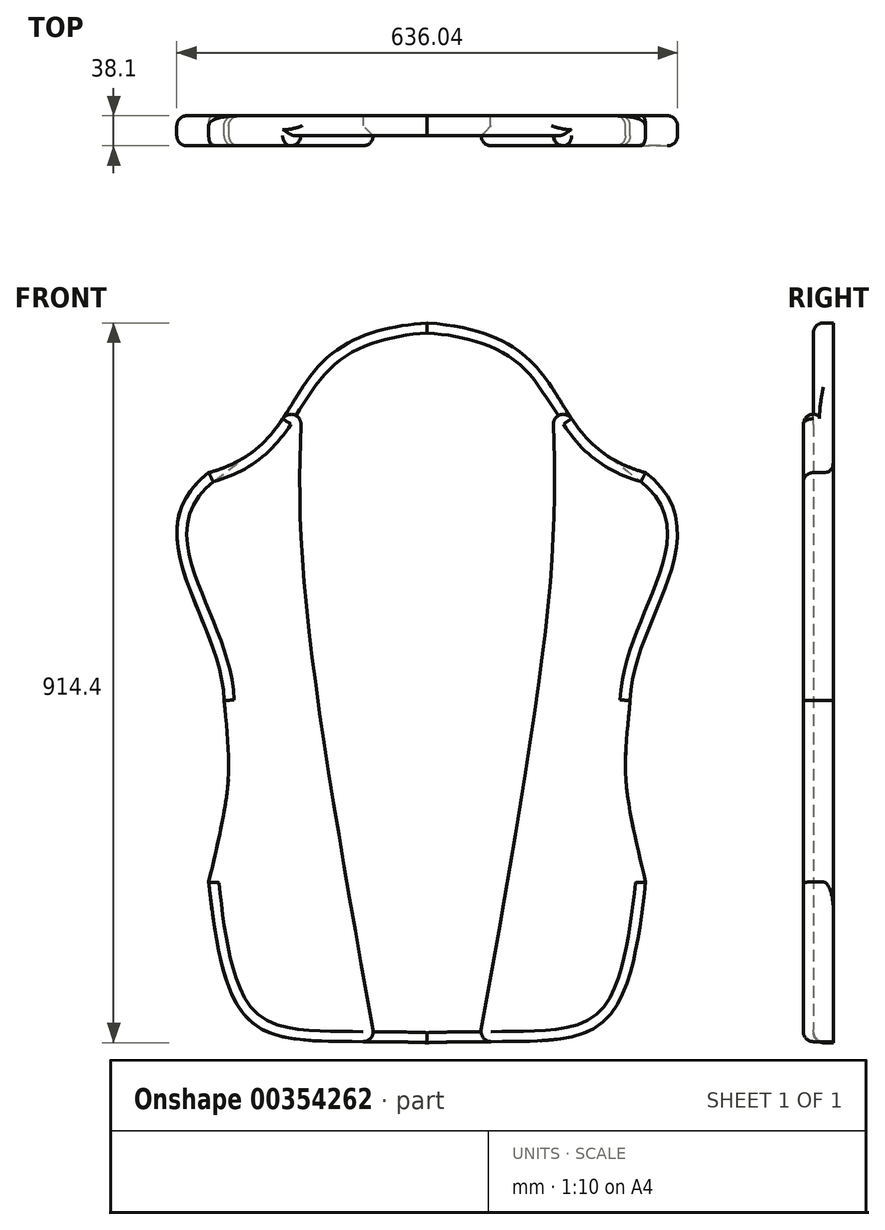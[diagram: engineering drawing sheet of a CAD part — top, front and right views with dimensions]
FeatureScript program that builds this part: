
annotation { "Feature Type Name" : "Feature", "Feature Type Description" : "" }
export const myFeature = defineFeature(function(context is Context, id is Id, definition is map)
    precondition{}
    {
        {
            var Q0;
            Q0=qCreatedBy(makeId("Front.planeOp"),FACE);
            var sketch = newSketch(context, id + "F0", { "sketchPlane" : qUnion([Q0])});
            skFitSpline(sketch, "E0", {"points": [v(0, -336.62) * mm, v(-277.45, -132.55) * mm], "startDerivative": vector(-633.05, 22.6) * mm, "endDerivative": vector(-75.36, 708.4) * mm});
            skFitSpline(sketch, "E1", {"points": [v(-277.45, -132.55) * mm, v(-257.9, 97.97) * mm], "startDerivative": vector(90.44, 384.35) * mm, "endDerivative": vector(-28.5, 293.91) * mm});
            skFitSpline(sketch, "E2", {"points": [v(-257.9, 97.97) * mm, v(-277.45, 387.49) * mm], "startDerivative": vector(-7.54, 308.99) * mm, "endDerivative": vector(301.45, 233.62) * mm});
            skFitSpline(sketch, "E3", {"points": [v(-277.45, 387.49) * mm, v(0, 577.78) * mm], "startDerivative": vector(428.8, 118.6) * mm, "endDerivative": vector(606.67, 45.22) * mm});
            skLineSegment(sketch, "E4", {"start": v(0, 700.87) * mm, "end": v(0, -462.22) * mm, "construction": true});
            skFitSpline(sketch, "E5.MirrorCS", {"points": [v(277.45, 387.49) * mm, v(0, 577.78) * mm], "startDerivative": vector(-428.8, 118.6) * mm, "endDerivative": vector(-606.67, 45.22) * mm});
            skFitSpline(sketch, "E6.MirrorCS", {"points": [v(257.9, 97.97) * mm, v(277.45, 387.49) * mm], "startDerivative": vector(7.54, 308.99) * mm, "endDerivative": vector(-301.45, 233.62) * mm});
            skFitSpline(sketch, "E7.MirrorCS", {"points": [v(277.45, -132.55) * mm, v(257.9, 97.97) * mm], "startDerivative": vector(-90.44, 384.35) * mm, "endDerivative": vector(28.5, 293.91) * mm});
            skFitSpline(sketch, "E8.MirrorCS", {"points": [v(0, -336.62) * mm, v(277.45, -132.55) * mm], "startDerivative": vector(633.05, 22.6) * mm, "endDerivative": vector(75.36, 708.4) * mm});
            skFitSpline(sketch, "E9", {"points": [v(-158.07, 496.23) * mm, v(-157.28, 260.19) * mm, v(-66.01, -335.4) * mm], "startDerivative": vector(-27, -544.47) * mm, "endDerivative": vector(193.6, -1077.9) * mm});
            skFitSpline(sketch, "E10.MirrorCS", {"points": [v(158.07, 496.23) * mm, v(157.28, 260.19) * mm, v(66.01, -335.4) * mm], "startDerivative": vector(27, -544.47) * mm, "endDerivative": vector(-193.6, -1077.9) * mm});
            skSolve(sketch);
        }
        {
            var Q0;
            {var subQ7=sQuery(id+"F0.wireOp",EDGE,"E9");Q0=makeQuery(id+"F0.imprint","IMPRINT",FACE,{"disambiguationData":[TD([[makeQuery(id+"F0.imprint","IMPRINT",EDGE,{"derivedFrom":subQ7}),1.0]])]});}
            extrude(context, id + "F1", {"entities" : qUnion([Q0]), "depth" : 25.4 * mm});
        }
        {
            var Q0;
            {var subQ3=sQuery(id+"F0.wireOp",EDGE,"E1");Q0=makeQuery(id+"F0.imprint","IMPRINT",FACE,{"disambiguationData":[TD([[makeQuery(id+"F0.imprint","IMPRINT",EDGE,{"derivedFrom":subQ3}),-1.0]])]});}
            var Q1;
            {var subQ1=sQuery(id+"F0.wireOp",EDGE,"E6.MirrorCS");Q1=makeQuery(id+"F0.imprint","IMPRINT",FACE,{"disambiguationData":[TD([[makeQuery(id+"F0.imprint","IMPRINT",EDGE,{"derivedFrom":subQ1}),1.0]])]});}
            extrude(context, id + "F2", {"entities" : qUnion([Q0, Q1]), "operationType" : NewBodyOperationType.ADD, "depth" : 38.1 * mm});
        }
        {
            var Q0;
            Q0=makeQuery(id+"F2.opExtrude","CAP_EDGE",EDGE,{"disambiguationData":[OSD([sQuery(id+"F0.wireOp",EDGE,"E3")])],"isStart":false});
            var Q1;
            Q1=makeQuery(id+"F2.opExtrude","CAP_EDGE",EDGE,{"disambiguationData":[OSD([sQuery(id+"F0.wireOp",EDGE,"E2")])],"isStart":false});
            var Q2;
            Q2=makeQuery(id+"F2.opExtrude","CAP_EDGE",EDGE,{"disambiguationData":[OSD([sQuery(id+"F0.wireOp",EDGE,"E1")])],"isStart":false});
            var Q3;
            Q3=makeQuery(id+"F2.opExtrude","CAP_EDGE",EDGE,{"disambiguationData":[OSD([sQuery(id+"F0.wireOp",EDGE,"E0")])],"isStart":false});
            var Q4;
            Q4=makeQuery(id+"F1.opExtrude","CAP_EDGE",EDGE,{"disambiguationData":[OSD([sQuery(id+"F0.wireOp",EDGE,"E0")])],"isStart":false});
            var Q5;
            Q5=makeQuery(id+"F1.opExtrude","CAP_EDGE",EDGE,{"disambiguationData":[OSD([sQuery(id+"F0.wireOp",EDGE,"E8.MirrorCS")])],"isStart":false});
            var Q6;
            Q6=makeQuery(id+"F2.opExtrude","CAP_EDGE",EDGE,{"disambiguationData":[OSD([sQuery(id+"F0.wireOp",EDGE,"E8.MirrorCS")])],"isStart":false});
            var Q7;
            Q7=makeQuery(id+"F2.opExtrude","CAP_EDGE",EDGE,{"disambiguationData":[OSD([sQuery(id+"F0.wireOp",EDGE,"E7.MirrorCS")])],"isStart":false});
            var Q8;
            Q8=makeQuery(id+"F2.opExtrude","CAP_EDGE",EDGE,{"disambiguationData":[OSD([sQuery(id+"F0.wireOp",EDGE,"E6.MirrorCS")])],"isStart":false});
            var Q9;
            Q9=makeQuery(id+"F2.opExtrude","CAP_EDGE",EDGE,{"disambiguationData":[OSD([sQuery(id+"F0.wireOp",EDGE,"E5.MirrorCS")])],"isStart":false});
            var Q10;
            Q10=makeQuery(id+"F1.opExtrude","CAP_EDGE",EDGE,{"disambiguationData":[OSD([sQuery(id+"F0.wireOp",EDGE,"E5.MirrorCS")])],"isStart":false});
            var Q11;
            Q11=makeQuery(id+"F1.opExtrude","CAP_EDGE",EDGE,{"disambiguationData":[OSD([sQuery(id+"F0.wireOp",EDGE,"E3")])],"isStart":false});
            var Q12;
            {var subQ0=sQuery(id+"F0.wireOp",EDGE,"E8.MirrorCS");Q12=makeQuery(id+"F2.boolean.opBoolean","MERGE",EDGE,{"derivedFrom":[makeQuery(id+"F1.opExtrude","CAP_EDGE",EDGE,{"disambiguationData":[OSD([subQ0])],"isStart":true}),makeQuery(id+"F2.opExtrude","CAP_EDGE",EDGE,{"disambiguationData":[OSD([subQ0])],"isStart":true})]});}
            var Q13;
            Q13=makeQuery(id+"F2.opExtrude","CAP_EDGE",EDGE,{"disambiguationData":[OSD([sQuery(id+"F0.wireOp",EDGE,"E7.MirrorCS")])],"isStart":true});
            var Q14;
            Q14=makeQuery(id+"F2.opExtrude","CAP_EDGE",EDGE,{"disambiguationData":[OSD([sQuery(id+"F0.wireOp",EDGE,"E6.MirrorCS")])],"isStart":true});
            var Q15;
            {var subQ0=sQuery(id+"F0.wireOp",EDGE,"E5.MirrorCS");Q15=makeQuery(id+"F2.boolean.opBoolean","MERGE",EDGE,{"derivedFrom":[makeQuery(id+"F1.opExtrude","CAP_EDGE",EDGE,{"disambiguationData":[OSD([subQ0])],"isStart":true}),makeQuery(id+"F2.opExtrude","CAP_EDGE",EDGE,{"disambiguationData":[OSD([subQ0])],"isStart":true})]});}
            var Q16;
            {var subQ0=sQuery(id+"F0.wireOp",EDGE,"E3");Q16=makeQuery(id+"F2.boolean.opBoolean","MERGE",EDGE,{"derivedFrom":[makeQuery(id+"F1.opExtrude","CAP_EDGE",EDGE,{"disambiguationData":[OSD([subQ0])],"isStart":true}),makeQuery(id+"F2.opExtrude","CAP_EDGE",EDGE,{"disambiguationData":[OSD([subQ0])],"isStart":true})]});}
            var Q17;
            Q17=makeQuery(id+"F2.opExtrude","CAP_EDGE",EDGE,{"disambiguationData":[OSD([sQuery(id+"F0.wireOp",EDGE,"E2")])],"isStart":true});
            var Q18;
            Q18=makeQuery(id+"F2.opExtrude","CAP_EDGE",EDGE,{"disambiguationData":[OSD([sQuery(id+"F0.wireOp",EDGE,"E1")])],"isStart":true});
            var Q19;
            {var subQ0=sQuery(id+"F0.wireOp",EDGE,"E0");Q19=makeQuery(id+"F2.boolean.opBoolean","MERGE",EDGE,{"derivedFrom":[makeQuery(id+"F1.opExtrude","CAP_EDGE",EDGE,{"disambiguationData":[OSD([subQ0])],"isStart":true}),makeQuery(id+"F2.opExtrude","CAP_EDGE",EDGE,{"disambiguationData":[OSD([subQ0])],"isStart":true})]});}
            fillet(context, id + "F3", {"entities" : qUnion([Q0, Q1, Q2, Q3, Q4, Q5, Q6, Q7, Q8, Q9, Q10, Q11, Q12, Q13, Q14, Q15, Q16, Q17, Q18, Q19]), "radius" : 12.7 * mm, "tangentPropagation" : true, "allowEdgeOverflow" : false});
        }
        {
            var Q0;
            Q0=makeQuery(id+"F2.opExtrude","CAP_EDGE",EDGE,{"disambiguationData":[OSD([sQuery(id+"F0.wireOp",EDGE,"E9")])],"isStart":false});
            var Q1;
            Q1=makeQuery(id+"F2.opExtrude","CAP_EDGE",EDGE,{"disambiguationData":[OSD([sQuery(id+"F0.wireOp",EDGE,"E10.MirrorCS")])],"isStart":false});
            fillet(context, id + "F4", {"entities" : qUnion([Q0, Q1]), "radius" : 12.7 * mm, "tangentPropagation" : true, "allowEdgeOverflow" : false});
        }
    });
